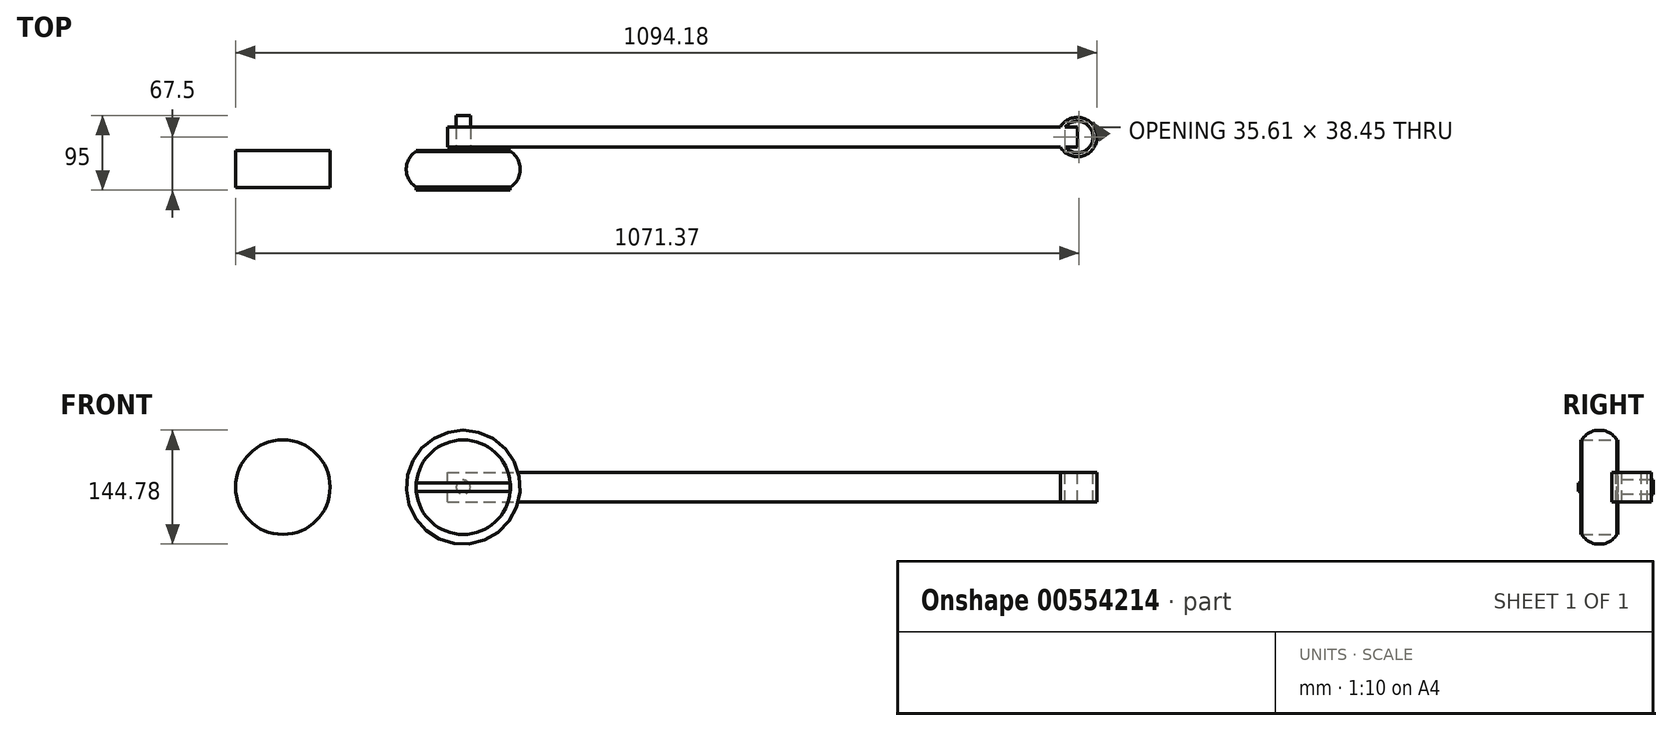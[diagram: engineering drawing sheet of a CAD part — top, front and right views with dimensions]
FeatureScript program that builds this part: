
annotation { "Feature Type Name" : "Feature", "Feature Type Description" : "" }
export const myFeature = defineFeature(function(context is Context, id is Id, definition is map)
    precondition{}
    {
        {
            var Q0;
            Q0=qCreatedBy(makeId("Front.planeOp"),FACE);
            var sketch = newSketch(context, id + "F0", { "sketchPlane" : qUnion([Q0])});
            skCircle(sketch, "E0", {"center": v(0, 0) * mm, "radius": 60 * mm});
            skSolve(sketch);
        }
        {
            var Q0;
            Q0=qCreatedBy(makeId("Front.planeOp"),FACE);
            var sketch = newSketch(context, id + "F1", { "sketchPlane" : qUnion([Q0])});
            skCircle(sketch, "E1", {"center": v(-229.18, 0) * mm, "radius": 60 * mm});
            skSolve(sketch);
        }
        {
            var Q0;
            Q0=makeQuery(id+"F0.imprint","IMPRINT",FACE,{"disambiguationData":[TD([[makeQuery(id+"F0.imprint","IMPRINT",EDGE,{"derivedFrom":sQuery(id+"F0.wireOp",EDGE,"E0")}),1.0]])]});
            var Q1;
            Q1=makeQuery(id+"F1.imprint","IMPRINT",FACE,{"disambiguationData":[TD([[makeQuery(id+"F1.imprint","IMPRINT",EDGE,{"derivedFrom":sQuery(id+"F1.wireOp",EDGE,"E1")}),1.0]])]});
            extrude(context, id + "F2", {"entities" : qUnion([Q0, Q1]), "endBound" : BoundingType.SYMMETRIC, "depth" : 47 * mm, "offsetDistance" : 25 * mm});
        }
        {
            var Q0;
            Q0=qCreatedBy(makeId("Right.planeOp"),FACE);
            var sketch = newSketch(context, id + "F3", { "sketchPlane" : qUnion([Q0])});
            skLineSegment(sketch, "E2.bottom", {"start": v(119.87, 0) * mm, "end": v(-127.87, 0) * mm});
            skLineSegment(sketch, "E2.top", {"start": v(119.87, 253.48) * mm, "end": v(-127.87, 253.48) * mm});
            skLineSegment(sketch, "E2.left", {"start": v(119.87, 0) * mm, "end": v(119.87, 253.48) * mm});
            skLineSegment(sketch, "E2.right", {"start": v(-127.87, 0) * mm, "end": v(-127.87, 253.48) * mm});
            skLineSegment(sketch, "E3.bottom", {"start": v(-40, 60) * mm, "end": v(40, 60) * mm});
            skLineSegment(sketch, "E3.top", {"start": v(-40, -60) * mm, "end": v(40, -60) * mm});
            skLineSegment(sketch, "E3.left", {"start": v(-40, 60) * mm, "end": v(-40, -60) * mm});
            skLineSegment(sketch, "E3.right", {"start": v(40, 60) * mm, "end": v(40, -60) * mm});
            skPoint(sketch, "E3.middle", {"position": v(0, 0) * mm});
            skSolve(sketch);
        }
        {
            var Q0;
            Q0=makeQuery(id+"F3.imprint","IMPRINT",FACE,{"disambiguationData":[TD([[makeQuery(id+"F3.imprint","IMPRINT",EDGE,{"derivedFrom":sQuery(id+"F3.wireOp",EDGE,"E2.top")}),1.0]])]});
            var sketch = newSketch(context, id + "F4", { "sketchPlane" : qUnion([Q0])});
            skCircle(sketch, "E4", {"center": v(0, 45.72) * mm, "radius": 26.67 * mm});
            skSolve(sketch);
        }
        {
            var Q0;
            {var subQ0=sQuery(id+"F4.wireOp",EDGE,"E4");var subQ1=makeQuery(id+"F3.imprint","IMPRINT",EDGE,{"derivedFrom":sQuery(id+"F3.wireOp",EDGE,"E3.bottom")});var subQ2=makeQuery(id+"F4.imprint","INTERSECT",VERTEX,{"disambiguationData":[OD(0.0)],"derivedFrom":[subQ1,subQ0]});Q0=makeQuery(id+"F4.imprint","IMPRINT",FACE,{"disambiguationData":[TD([[makeQuery(id+"F4.imprint","IMPRINT",EDGE,{"disambiguationData":[TD([[subQ2,1.0]])],"derivedFrom":subQ0}),1.0]])]});}
            var Q1;
            Q1=sQuery(id+"F3.wireOp",EDGE,"E2.bottom");
            revolve(context, id + "F5", {"operationType" : NewBodyOperationType.ADD, "entities" : qUnion([Q0]), "axis" : qUnion([Q1]), "revolveType" : RevolveType.FULL});
        }
        {
            var Q0;
            Q0=makeQuery(id+"F2.opExtrude","CAP_FACE",FACE,{"disambiguationData":[OSD([sQuery(id+"F0.wireOp",EDGE,"E0")])],"isStart":true});
            var sketch = newSketch(context, id + "F6", { "sketchPlane" : qUnion([Q0])});
            skCircle(sketch, "E5", {"center": v(0, 0) * mm, "radius": 9 * mm});
            skSolve(sketch);
        }
        {
            var Q0;
            Q0=makeQuery(id+"F6.imprint","IMPRINT",FACE,{"disambiguationData":[TD([[makeQuery(id+"F6.imprint","IMPRINT",EDGE,{"derivedFrom":sQuery(id+"F6.wireOp",EDGE,"E5")}),1.0]])]});
            extrude(context, id + "F7", {"entities" : qUnion([Q0]), "operationType" : NewBodyOperationType.ADD, "depth" : 45 * mm, "offsetDistance" : 25 * mm});
        }
        {
            var Q0;
            Q0=makeQuery(id+"F2.opExtrude","CAP_FACE",FACE,{"disambiguationData":[OSD([sQuery(id+"F0.wireOp",EDGE,"E0")])],"isStart":true});
            cPlane(context, id + "F8", {"entities" : qUnion([Q0]), "cplaneType" : CPlaneType.OFFSET, "offset" : 5 * mm, "width" : 150 * mm, "height" : 150 * mm});
        }
        {
            var Q0;
            Q0=qCreatedBy(id+"F8.planeOp",FACE);
            var sketch = newSketch(context, id + "F9", { "sketchPlane" : qUnion([Q0])});
            skLineSegment(sketch, "E6.bottom", {"start": v(20, -19) * mm, "end": v(-780, -19) * mm});
            skLineSegment(sketch, "E6.top", {"start": v(20, 19) * mm, "end": v(-780, 19) * mm});
            skLineSegment(sketch, "E6.left", {"start": v(20, -19) * mm, "end": v(20, 19) * mm});
            skLineSegment(sketch, "E6.right", {"start": v(-780, -19) * mm, "end": v(-780, 19) * mm});
            skPoint(sketch, "E6.middle", {"position": v(-380, 0) * mm});
            skSolve(sketch);
        }
        {
            var Q0;
            Q0 = qSketchRegion(id + "F9", true);
            extrude(context, id + "F10", {"entities" : qUnion([Q0]), "depth" : 25 * mm, "offsetDistance" : 25 * mm});
        }
        {
            var Q0;
            Q0=makeQuery(id+"F10.opExtrude","SWEPT_FACE",FACE,{"disambiguationData":[OSD([sQuery(id+"F9.wireOp",EDGE,"E6.top")])]});
            var sketch = newSketch(context, id + "F11", { "sketchPlane" : qUnion([Q0])});
            skCircle(sketch, "E7", {"center": v(780, 41) * mm, "radius": 25 * mm});
            skCircle(sketch, "E8.0", {"center": v(780, 41) * mm, "radius": 20 * mm});
            skSolve(sketch);
        }
        {
            var Q0;
            {var subQ0=sQuery(id+"F11.wireOp",EDGE,"E7");var subQ1=sQuery(id+"F9.wireOp",EDGE,"E6.top");var subQ2=makeQuery(id+"F10.opExtrude","CAP_EDGE",EDGE,{"disambiguationData":[OSD([subQ1])],"isStart":true});var subQ3=makeQuery(id+"F11.imprint","INTERSECT",VERTEX,{"derivedFrom":[subQ2,subQ0]});Q0=makeQuery(id+"F11.imprint","IMPRINT",FACE,{"disambiguationData":[TD([[makeQuery(id+"F11.imprint","IMPRINT",EDGE,{"disambiguationData":[TD([[subQ3,-1.0]])],"derivedFrom":subQ0}),1.0]])]});}
            extrude(context, id + "F12", {"entities" : qUnion([Q0]), "operationType" : NewBodyOperationType.ADD, "oppositeDirection" : true, "depth" : 38 * mm, "offsetDistance" : 25 * mm});
        }
        {
            var Q0;
            Q0=makeQuery(id+"F2.opExtrude","CAP_FACE",FACE,{"disambiguationData":[OSD([sQuery(id+"F0.wireOp",EDGE,"E0")])],"isStart":false});
            var sketch = newSketch(context, id + "F13", { "sketchPlane" : qUnion([Q0])});
            skLineSegment(sketch, "E9.bottom", {"start": v(59.73, -5.64) * mm, "end": v(-59.73, -5.64) * mm});
            skLineSegment(sketch, "E9.top", {"start": v(59.73, 5.64) * mm, "end": v(-59.73, 5.64) * mm});
            skLineSegment(sketch, "E9.left", {"start": v(59.73, -5.64) * mm, "end": v(59.73, 5.64) * mm});
            skLineSegment(sketch, "E9.right", {"start": v(-59.73, -5.64) * mm, "end": v(-59.73, 5.64) * mm});
            skPoint(sketch, "E9.middle", {"position": v(0, 0) * mm});
            skSolve(sketch);
        }
        {
            var Q0;
            Q0=makeQuery(id+"F13.imprint","IMPRINT",FACE,{"disambiguationData":[TD([[makeQuery(id+"F13.imprint","IMPRINT",EDGE,{"derivedFrom":sQuery(id+"F13.wireOp",EDGE,"E9.bottom")}),-1.0]])]});
            extrude(context, id + "F14", {"entities" : qUnion([Q0]), "operationType" : NewBodyOperationType.ADD, "depth" : 3 * mm, "offsetDistance" : 25 * mm});
        }
    });
